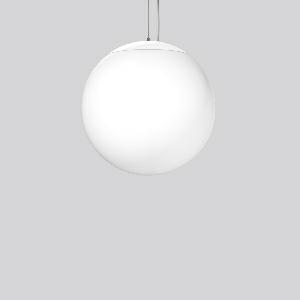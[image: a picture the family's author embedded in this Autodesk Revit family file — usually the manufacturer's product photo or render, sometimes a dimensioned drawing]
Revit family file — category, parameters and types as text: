
# Revit family: basic_ball_312095_002_1_76_8e3a
name_source: partatom
category: Lighting Fixtures
units: mm (PartAtom-declared; Revit-internal decimal feet)

## family parameters
Cut with Voids When Loaded = No
Host = Face
Light Source = No
Part Type = Normal
Room Calculation Point = No
Round Connector Dimension = Use Diameter
Shared = No

## types (1)
- BASIC BALL (1 x LED Modul 940, 8850 lm, 4000)
    Apparent Load = 79 VA
    CIE Flux Codes = 25 50 75 55 100
    Color Rendering = 92
    Color Temperature = 4000
    Default Elevation = 1800 mm
    Description = Series: BASIC BALL
Pendant luminaire in timelessly classic sphere design. Canopy: metal, powder-coated, white. Metal cap: white, powder-coated. Diffuser: mouth-blown opal glass, satin finish. Shadow-free, homogeneous and soft illumination. Single-point steel cable suspension, steplessly adjustable. Special lengths available on request. Power supply cable: white. 
Colour: white
Diameter: 400 mm
Height: 400 mm
Suspension length: 300-4000 mm
Lamp: LED
Socket: without socket
Colour temperature: 4000K
Colour rendering index (CRI): 90
System power: 79 W
Rated luminous flux: 8850 lm
Luminous efficiency: 112 lm/W
Control gear: Converter, dimmable, DALI
Protection class: I
Type of protection: IP 40
    Height = 400 mm
    Lamp = 1 x LED Modul 940
    Lamp Light Flux = 8850 lm
    Lamp count = 1
    Length = 400 mm
    Lifetime = 50000 h
    Luminous efficacy = 112 lm/W
    Manufacturer = RZB
    ModVariant = No
    Model = 312095.002.1.76
    Mounting Place = Ceiling
    Mounting Type = Pendant
    Number of Poles = 1
    OnlyDefault = Yes
    Power Factor = 1
    Product Name = BASIC BALL
    Product group = Pendant luminaires
    ProductGroupID = 902
    Protection Class = Protection class I
    Protection Degree = IP 40
    RLX_Detail_Level = 1
    RLX_Emergency_Light_Flux = 0 lm
    RLX_Emergency_Type = 0
    RLX_Emergency_Type_DB = No
    RlxData = <blob elided: 53853 chars, md5=71ea4161>
    Socket = socket
    Standby Power = 0 W
    System Light Flux = 8850 lm
    System Power = 79 W
    Type Comments = Product without accessories
    Type Image = 312095.002.jpg
    URL = http://relux.com
    VarID = ---
    Voltage = 230 V
    Voltage Range = 220-240 V
    Weight = 0.00 kg
    Width = 0 mm  [stored 0 ft]

note: [stored X ft] marks values corroborated as IEEE doubles in the binary element streams (Revit-internal decimal feet)

## geometry (parser evidence)
native form markers: Blend x4, Sweep x12
no freeform markers — native parametric forms only
